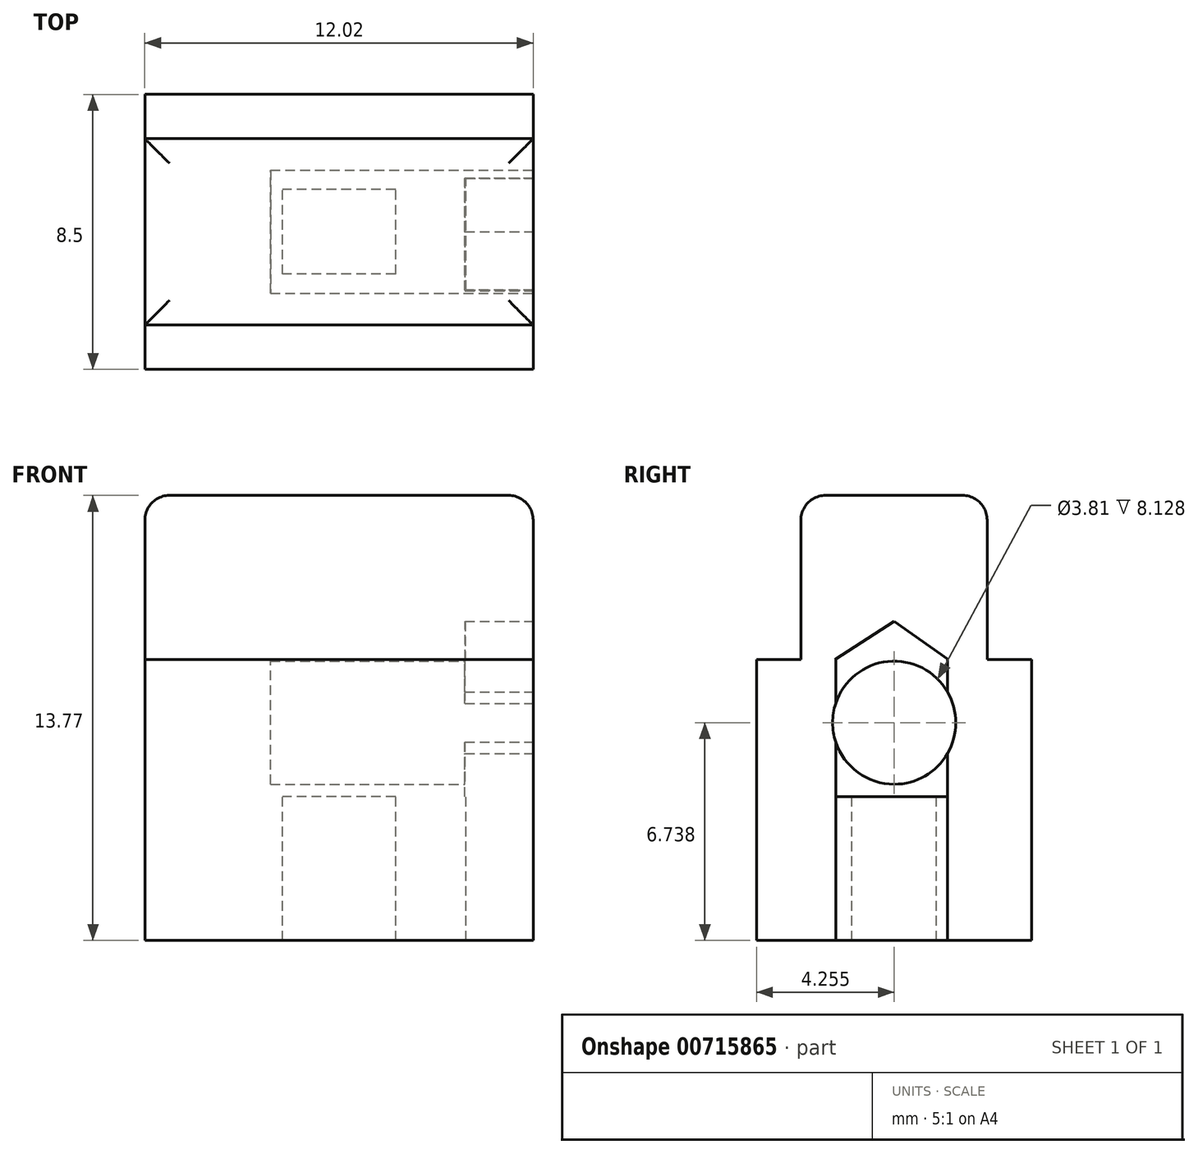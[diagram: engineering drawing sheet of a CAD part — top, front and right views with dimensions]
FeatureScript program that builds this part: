
annotation { "Feature Type Name" : "Feature", "Feature Type Description" : "" }
export const myFeature = defineFeature(function(context is Context, id is Id, definition is map)
    precondition{}
    {
        {
            var Q0;
            Q0=qCreatedBy(makeId("Top.planeOp"),FACE);
            var sketch = newSketch(context, id + "F0", { "sketchPlane" : qUnion([Q0])});
            skLineSegment(sketch, "E0.bottom", {"start": v(6, 2.88) * mm, "end": v(-6, 2.88) * mm});
            skLineSegment(sketch, "E0.top", {"start": v(6, -2.88) * mm, "end": v(-6, -2.88) * mm});
            skLineSegment(sketch, "E0.left", {"start": v(6, 2.88) * mm, "end": v(6, -2.88) * mm});
            skLineSegment(sketch, "E0.right", {"start": v(-6, 2.88) * mm, "end": v(-6, -2.88) * mm});
            skPoint(sketch, "E0.middle", {"position": v(0, 0) * mm});
            skSolve(sketch);
        }
        {
            var Q0;
            Q0=makeQuery(id+"F0.imprint","IMPRINT",FACE,{"disambiguationData":[TD([[makeQuery(id+"F0.imprint","IMPRINT",EDGE,{"derivedFrom":sQuery(id+"F0.wireOp",EDGE,"E0.bottom")}),1.0]])]});
            extrude(context, id + "F1", {"entities" : qUnion([Q0]), "depth" : 5.08 * mm, "offsetDistance" : 25.4 * mm});
        }
        {
            var Q0;
            Q0=qCreatedBy(makeId("Top.planeOp"),FACE);
            var sketch = newSketch(context, id + "F2", { "sketchPlane" : qUnion([Q0])});
            skLineSegment(sketch, "E1.bottom", {"start": v(6, -4.25) * mm, "end": v(-6, -4.25) * mm});
            skLineSegment(sketch, "E1.top", {"start": v(6, 4.25) * mm, "end": v(-6, 4.25) * mm});
            skLineSegment(sketch, "E1.left", {"start": v(6, -4.25) * mm, "end": v(6, 4.25) * mm});
            skLineSegment(sketch, "E1.right", {"start": v(-6, -4.25) * mm, "end": v(-6, 4.25) * mm});
            skPoint(sketch, "E1.middle", {"position": v(0, 0) * mm});
            skSolve(sketch);
        }
        {
            var Q0;
            Q0=makeQuery(id+"F2.imprint","IMPRINT",FACE,{"disambiguationData":[TD([[makeQuery(id+"F2.imprint","IMPRINT",EDGE,{"derivedFrom":sQuery(id+"F2.wireOp",EDGE,"E1.bottom")}),-1.0]])]});
            extrude(context, id + "F3", {"entities" : qUnion([Q0]), "operationType" : NewBodyOperationType.ADD, "oppositeDirection" : true, "depth" : 4.24 * mm, "offsetDistance" : 25.4 * mm});
        }
        {
            var Q0;
            Q0=makeQuery(id+"F1.opExtrude","CAP_FACE",FACE,{"disambiguationData":[OSD([sQuery(id+"F0.wireOp",EDGE,"E0.bottom"),sQuery(id+"F0.wireOp",EDGE,"E0.top"),sQuery(id+"F0.wireOp",EDGE,"E0.left"),sQuery(id+"F0.wireOp",EDGE,"E0.right")])],"isStart":false});
            fillet(context, id + "F4", {"entities" : qUnion([Q0]), "radius" : 0.76 * mm, "tangentPropagation" : true, "allowEdgeOverflow" : false});
        }
        {
            var Q0;
            Q0=qCreatedBy(makeId("Right.planeOp"),FACE);
            var Q1;
            Q1=makeQuery(id+"F3.opExtrude","CAP_EDGE",EDGE,{"disambiguationData":[OSD([sQuery(id+"F2.wireOp",EDGE,"E1.left")])],"isStart":false});
            cPlane(context, id + "F5", {"entities" : qUnion([Q0, Q1]), "cplaneType" : CPlaneType.LINE_ANGLE, "offset" : 25.4 * mm, "angle" : 180 * degree, "width" : 152.4 * mm, "height" : 152.4 * mm});
        }
        {
            var Q0;
            Q0=qCreatedBy(id+"F5.planeOp",FACE);
            var sketch = newSketch(context, id + "F6", { "sketchPlane" : qUnion([Q0])});
            skPoint(sketch, "E2.middle", {"position": v(0, -1.95) * mm});
            skCircle(sketch, "E3", {"center": v(0, -1.95) * mm, "radius": 1.9 * mm});
            skSolve(sketch);
        }
        {
            var Q0;
            Q0 = qSketchRegion(id + "F6", true);
            extrude(context, id + "F7", {"entities" : qUnion([Q0]), "operationType" : NewBodyOperationType.REMOVE, "oppositeDirection" : true, "depth" : 8.13 * mm, "offsetDistance" : 25.4 * mm});
        }
        {
            var Q0;
            Q0=qCreatedBy(makeId("Top.planeOp"),FACE);
            var sketch = newSketch(context, id + "F8", { "sketchPlane" : qUnion([Q0])});
            skLineSegment(sketch, "E4.bottom", {"start": v(6.04, -1.8) * mm, "end": v(3.9, -1.8) * mm});
            skLineSegment(sketch, "E4.top", {"start": v(6.04, 1.66) * mm, "end": v(3.9, 1.66) * mm});
            skLineSegment(sketch, "E4.left", {"start": v(6.04, -1.8) * mm, "end": v(6.04, 1.66) * mm});
            skLineSegment(sketch, "E4.right", {"start": v(3.9, -1.8) * mm, "end": v(3.9, 1.66) * mm});
            skSolve(sketch);
        }
        {
            var Q0;
            Q0 = qSketchRegion(id + "F8", true);
            extrude(context, id + "F9", {"entities" : qUnion([Q0]), "operationType" : NewBodyOperationType.REMOVE, "oppositeDirection" : true, "depth" : 25.4 * mm, "offsetDistance" : 25.4 * mm});
        }
        {
            var Q0;
            Q0=qCreatedBy(makeId("Top.planeOp"),FACE);
            cPlane(context, id + "F10", {"entities" : qUnion([Q0]), "cplaneType" : CPlaneType.OFFSET, "offset" : 4.24 * mm, "oppositeDirection" : true, "width" : 152.4 * mm, "height" : 152.4 * mm});
        }
        {
            var Q0;
            Q0=qCreatedBy(id+"F10.planeOp",FACE);
            var sketch = newSketch(context, id + "F11", { "sketchPlane" : qUnion([Q0])});
            skLineSegment(sketch, "E5.bottom", {"start": v(1.75, -1.3) * mm, "end": v(-1.75, -1.3) * mm});
            skLineSegment(sketch, "E5.top", {"start": v(1.75, 1.3) * mm, "end": v(-1.75, 1.3) * mm});
            skLineSegment(sketch, "E5.left", {"start": v(1.75, -1.3) * mm, "end": v(1.75, 1.3) * mm});
            skLineSegment(sketch, "E5.right", {"start": v(-1.75, -1.3) * mm, "end": v(-1.75, 1.3) * mm});
            skPoint(sketch, "E5.middle", {"position": v(0, 0) * mm});
            skLineSegment(sketch, "E6.bottom", {"start": v(6, -4.25) * mm, "end": v(-6, -4.25) * mm});
            skLineSegment(sketch, "E6.top", {"start": v(6, 4.25) * mm, "end": v(-6, 4.25) * mm});
            skLineSegment(sketch, "E6.left", {"start": v(6, -4.25) * mm, "end": v(6, 4.25) * mm});
            skLineSegment(sketch, "E6.right", {"start": v(-6, -4.25) * mm, "end": v(-6, 4.25) * mm});
            skLineSegment(sketch, "E7.bottom", {"start": v(3.92, -1.8) * mm, "end": v(6, -1.8) * mm});
            skLineSegment(sketch, "E7.top", {"start": v(3.92, 1.66) * mm, "end": v(6, 1.66) * mm});
            skLineSegment(sketch, "E7.left", {"start": v(3.92, -1.8) * mm, "end": v(3.92, 1.66) * mm});
            skLineSegment(sketch, "E7.right", {"start": v(6, -1.8) * mm, "end": v(6, 1.66) * mm});
            skSolve(sketch);
        }
        {
            var Q0;
            Q0=makeQuery(id+"F11.imprint","IMPRINT",FACE,{"disambiguationData":[TD([[makeQuery(id+"F11.imprint","IMPRINT",EDGE,{"derivedFrom":sQuery(id+"F11.wireOp",EDGE,"E5.bottom")}),1.0]])]});
            extrude(context, id + "F12", {"entities" : qUnion([Q0]), "operationType" : NewBodyOperationType.ADD, "oppositeDirection" : true, "depth" : 4.44 * mm, "offsetDistance" : 25.4 * mm});
        }
        {
            var Q0;
            Q0=qCreatedBy(id+"F5.planeOp",FACE);
            var sketch = newSketch(context, id + "F13", { "sketchPlane" : qUnion([Q0])});
            skLineSegment(sketch, "E8", {"start": v(-1.82, 0) * mm, "end": v(0, 1.18) * mm});
            skLineSegment(sketch, "E9", {"start": v(0, 1.18) * mm, "end": v(1.67, 0) * mm});
            skLineSegment(sketch, "E10", {"start": v(1.67, 0) * mm, "end": v(-1.82, 0) * mm});
            skSolve(sketch);
        }
        {
            var Q0;
            Q0 = qSketchRegion(id + "F13", true);
            extrude(context, id + "F14", {"entities" : qUnion([Q0]), "operationType" : NewBodyOperationType.REMOVE, "oppositeDirection" : true, "depth" : 2.1 * mm, "offsetDistance" : 25.4 * mm});
        }
    });
